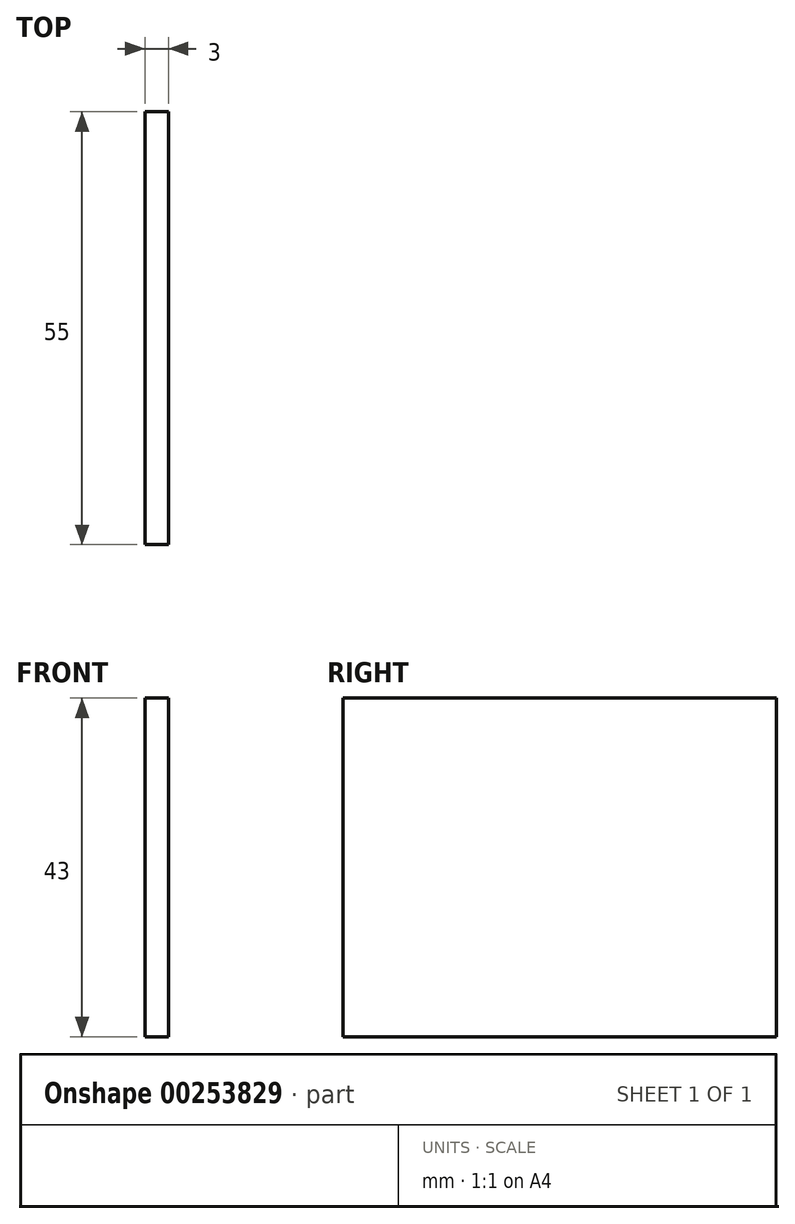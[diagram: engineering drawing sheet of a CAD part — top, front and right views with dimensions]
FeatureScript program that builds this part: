
annotation { "Feature Type Name" : "Feature", "Feature Type Description" : "" }
export const myFeature = defineFeature(function(context is Context, id is Id, definition is map)
    precondition{}
    {
        {
            var Q0;
            Q0=qCreatedBy(makeId("Right.planeOp"),FACE);
            var sketch = newSketch(context, id + "F0", { "sketchPlane" : qUnion([Q0])});
            skLineSegment(sketch, "E0", {"start": v(-27.5, -20) * mm, "end": v(27.5, -20) * mm});
            skLineSegment(sketch, "E1", {"start": v(27.5, -20) * mm, "end": v(27.5, 20) * mm});
            skLineSegment(sketch, "E2", {"start": v(27.5, 23) * mm, "end": v(-27.5, 23) * mm});
            skLineSegment(sketch, "E3", {"start": v(-27.5, 20) * mm, "end": v(-27.5, -20) * mm});
            skLineSegment(sketch, "E4", {"start": v(-27.5, 23) * mm, "end": v(-27.5, 20) * mm});
            skLineSegment(sketch, "E5", {"start": v(27.5, 23) * mm, "end": v(27.5, 20) * mm});
            skSolve(sketch);
        }
        {
            var Q0;
            Q0=makeQuery(id+"F0.imprint","IMPRINT",FACE,{"disambiguationData":[TD([[makeQuery(id+"F0.imprint","IMPRINT",EDGE,{"derivedFrom":sQuery(id+"F0.wireOp",EDGE,"E0")}),1.0]])]});
            extrude(context, id + "F1", {"entities" : qUnion([Q0]), "depth" : 3 * mm});
        }
    });
